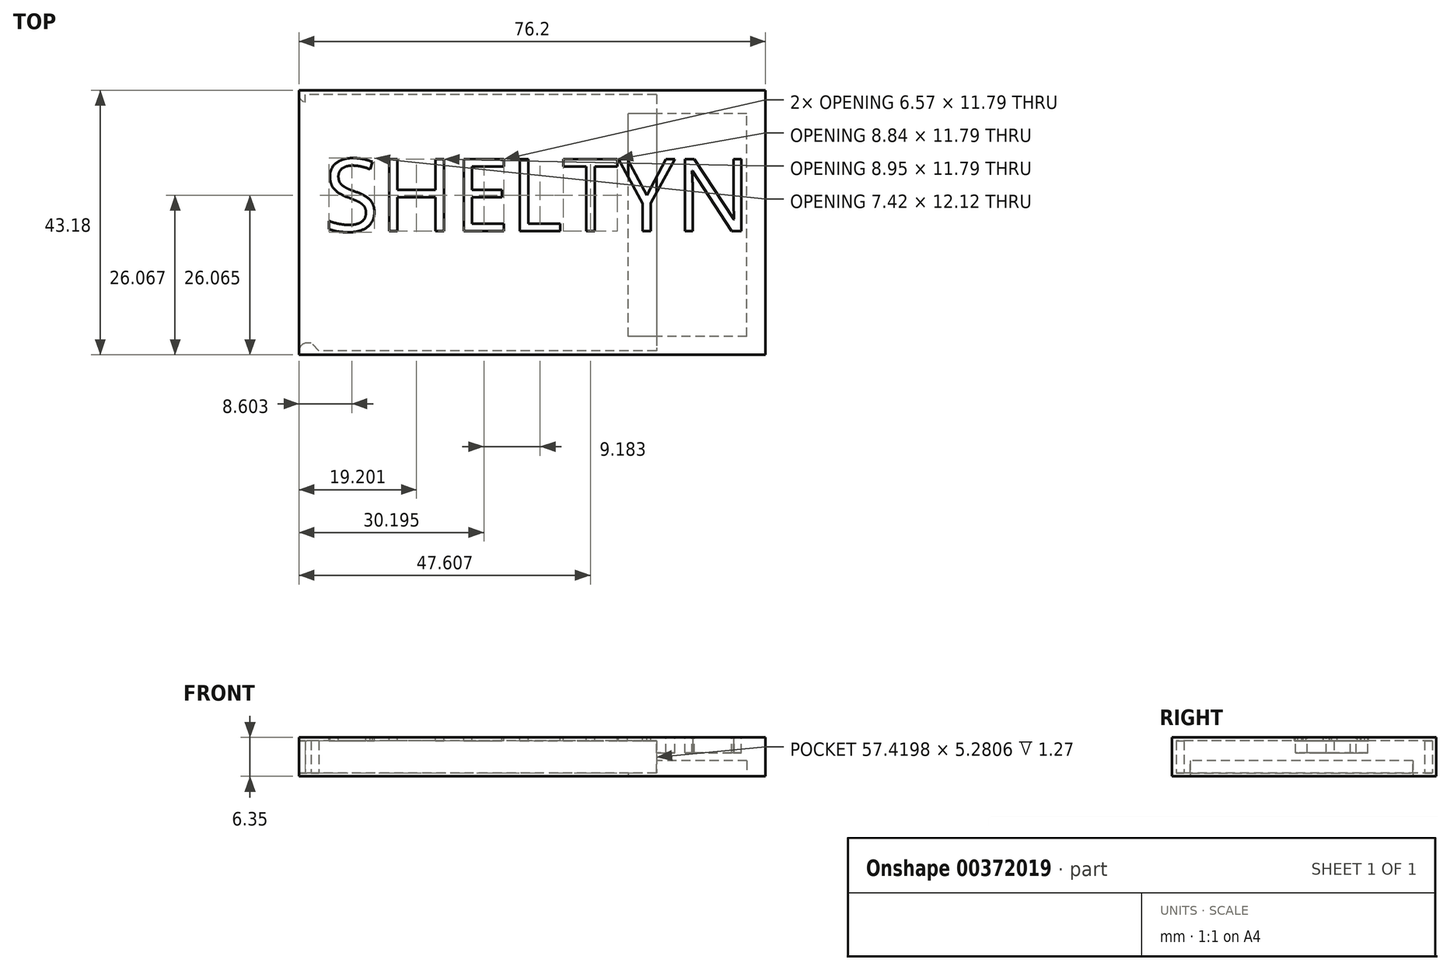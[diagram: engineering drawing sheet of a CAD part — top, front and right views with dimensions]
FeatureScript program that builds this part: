
annotation { "Feature Type Name" : "Feature", "Feature Type Description" : "" }
export const myFeature = defineFeature(function(context is Context, id is Id, definition is map)
    precondition{}
    {
        {
            var Q0;
            Q0=qCreatedBy(makeId("Top.planeOp"),FACE);
            var sketch = newSketch(context, id + "F0", { "sketchPlane" : qUnion([Q0])});
            skLineSegment(sketch, "E0.bottom", {"start": v(-35.13, 22.2) * mm, "end": v(41.07, 22.2) * mm});
            skLineSegment(sketch, "E0.top", {"start": v(-35.13, -20.99) * mm, "end": v(41.07, -20.99) * mm});
            skLineSegment(sketch, "E0.left", {"start": v(-35.13, 22.2) * mm, "end": v(-35.13, -20.99) * mm});
            skLineSegment(sketch, "E0.right", {"start": v(41.07, 22.2) * mm, "end": v(41.07, -20.99) * mm});
            skSolve(sketch);
        }
        {
            var Q0;
            Q0=makeQuery(id+"F0.imprint","IMPRINT",FACE,{"disambiguationData":[TD([[makeQuery(id+"F0.imprint","IMPRINT",EDGE,{"derivedFrom":sQuery(id+"F0.wireOp",EDGE,"E0.bottom")}),-1.0]])]});
            extrude(context, id + "F1", {"entities" : qUnion([Q0]), "depth" : 6.35 * mm});
        }
        {
            var Q0;
            Q0=makeQuery(id+"F1.opExtrude","SWEPT_FACE",FACE,{"disambiguationData":[OSD([sQuery(id+"F0.wireOp",EDGE,"E0.left")])]});
            var sketch = newSketch(context, id + "F2", { "sketchPlane" : qUnion([Q0])});
            skLineSegment(sketch, "E1.bottom", {"start": v(-21.5, 5.8) * mm, "end": v(20.34, 5.8) * mm});
            skLineSegment(sketch, "E1.top", {"start": v(-21.5, 0.5) * mm, "end": v(20.34, 0.5) * mm});
            skLineSegment(sketch, "E1.left", {"start": v(-21.5, 5.8) * mm, "end": v(-21.5, 0.5) * mm});
            skLineSegment(sketch, "E1.right", {"start": v(20.34, 5.8) * mm, "end": v(20.34, 0.5) * mm});
            skSolve(sketch);
        }
        {
            var Q0;
            Q0=makeQuery(id+"F2.imprint","IMPRINT",FACE,{"disambiguationData":[TD([[makeQuery(id+"F2.imprint","IMPRINT",EDGE,{"derivedFrom":sQuery(id+"F2.wireOp",EDGE,"E1.bottom")}),-1.0]])]});
            extrude(context, id + "F3", {"entities" : qUnion([Q0]), "operationType" : NewBodyOperationType.REMOVE, "oppositeDirection" : true, "depth" : 58.42 * mm});
        }
        {
            var Q0;
            Q0=makeQuery(id+"F1.opExtrude","CAP_FACE",FACE,{"disambiguationData":[OSD([sQuery(id+"F0.wireOp",EDGE,"E0.bottom"),sQuery(id+"F0.wireOp",EDGE,"E0.top"),sQuery(id+"F0.wireOp",EDGE,"E0.left"),sQuery(id+"F0.wireOp",EDGE,"E0.right")])],"isStart":true});
            var sketch = newSketch(context, id + "F4", { "sketchPlane" : qUnion([Q0])});
            skLineSegment(sketch, "E2.bottom", {"start": v(38.04, 18.01) * mm, "end": v(18.65, 18.01) * mm});
            skLineSegment(sketch, "E2.top", {"start": v(38.04, -18.38) * mm, "end": v(18.65, -18.38) * mm});
            skLineSegment(sketch, "E2.left", {"start": v(38.04, 18.01) * mm, "end": v(38.04, -18.38) * mm});
            skLineSegment(sketch, "E2.right", {"start": v(18.65, 18.01) * mm, "end": v(18.65, -18.38) * mm});
            skSolve(sketch);
        }
        {
            var Q0;
            Q0=makeQuery(id+"F4.imprint","IMPRINT",FACE,{"disambiguationData":[TD([[makeQuery(id+"F4.imprint","IMPRINT",EDGE,{"derivedFrom":sQuery(id+"F4.wireOp",EDGE,"E2.bottom")}),1.0]])]});
            extrude(context, id + "F5", {"entities" : qUnion([Q0]), "operationType" : NewBodyOperationType.REMOVE, "oppositeDirection" : true, "depth" : 2.54 * mm});
        }
        {
            var Q0;
            Q0=makeQuery(id+"F3.boolean.opBoolean","COPY",FACE,{"derivedFrom":makeQuery(id+"F3.opExtrude","SWEPT_FACE",FACE,{"disambiguationData":[OSD([sQuery(id+"F2.wireOp",EDGE,"E1.left")])]})});
            var sketch = newSketch(context, id + "F6", { "sketchPlane" : qUnion([Q0])});
            skLineSegment(sketch, "E3.bottom", {"start": v(-35.13, 5.8) * mm, "end": v(-34.13, 5.8) * mm});
            skLineSegment(sketch, "E3.top", {"start": v(-35.13, 0.5) * mm, "end": v(-34.13, 0.5) * mm});
            skLineSegment(sketch, "E3.left", {"start": v(-35.13, 5.8) * mm, "end": v(-35.13, 0.5) * mm});
            skLineSegment(sketch, "E3.right", {"start": v(-34.13, 5.8) * mm, "end": v(-34.13, 0.5) * mm});
            skSolve(sketch);
        }
        {
            var Q0;
            Q0=makeQuery(id+"F6.imprint","IMPRINT",FACE,{"disambiguationData":[TD([[makeQuery(id+"F6.imprint","IMPRINT",EDGE,{"derivedFrom":sQuery(id+"F6.wireOp",EDGE,"E3.bottom")}),1.0]])]});
            extrude(context, id + "F7", {"entities" : qUnion([Q0]), "operationType" : NewBodyOperationType.ADD, "depth" : 2.54 * mm});
        }
        {
            var Q0;
            Q0=makeQuery(id+"F7.opExtrude","CAP_EDGE",EDGE,{"disambiguationData":[OSD([sQuery(id+"F6.wireOp",EDGE,"E3.right")])],"isStart":false});
            chamfer(context, id + "F8", {"entities" : qUnion([Q0]), "width" : 1.27 * mm, "tangentPropagation" : true});
        }
        {
            var Q0;
            Q0=makeQuery(id+"F3.boolean.opBoolean","COPY",FACE,{"derivedFrom":makeQuery(id+"F3.opExtrude","SWEPT_FACE",FACE,{"disambiguationData":[OSD([sQuery(id+"F2.wireOp",EDGE,"E1.right")])]})});
            var sketch = newSketch(context, id + "F9", { "sketchPlane" : qUnion([Q0])});
            skLineSegment(sketch, "E4.bottom", {"start": v(35.13, 5.8) * mm, "end": v(31.88, 5.8) * mm});
            skLineSegment(sketch, "E4.top", {"start": v(35.13, 0.5) * mm, "end": v(31.88, 0.5) * mm});
            skLineSegment(sketch, "E4.left", {"start": v(35.13, 5.8) * mm, "end": v(35.13, 0.5) * mm});
            skLineSegment(sketch, "E4.right", {"start": v(31.88, 5.8) * mm, "end": v(31.88, 0.5) * mm});
            skSolve(sketch);
        }
        {
            var Q0;
            Q0=makeQuery(id+"F9.imprint","IMPRINT",FACE,{"disambiguationData":[TD([[makeQuery(id+"F9.imprint","IMPRINT",EDGE,{"derivedFrom":sQuery(id+"F9.wireOp",EDGE,"E4.bottom")}),-1.0]])]});
            extrude(context, id + "F10", {"entities" : qUnion([Q0]), "operationType" : NewBodyOperationType.ADD, "depth" : 1.27 * mm});
        }
        {
            var Q0;
            Q0=makeQuery(id+"F10.opExtrude","CAP_EDGE",EDGE,{"disambiguationData":[OSD([sQuery(id+"F9.wireOp",EDGE,"E4.right")])],"isStart":false});
            chamfer(context, id + "F11", {"entities" : qUnion([Q0]), "width" : 1.27 * mm, "tangentPropagation" : true});
        }
        {
            var Q0;
            Q0=makeQuery(id+"F8.opChamfer","BLEND_EDGE",EDGE,{"blendedFrom":[makeQuery(id+"F7.opExtrude","CAP_EDGE",EDGE,{"disambiguationData":[OSD([sQuery(id+"F6.wireOp",EDGE,"E3.right")])],"isStart":false}),makeQuery(id+"F7.boolean.opBoolean","MERGE",FACE,{"derivedFrom":[makeQuery(id+"F1.opExtrude","SWEPT_FACE",FACE,{"disambiguationData":[OSD([sQuery(id+"F0.wireOp",EDGE,"E0.left")])]}),makeQuery(id+"F7.opExtrude","SWEPT_FACE",FACE,{"disambiguationData":[OSD([sQuery(id+"F6.wireOp",EDGE,"E3.left")])]})]})],"blendedInto":[makeQuery(id+"F7.boolean.opBoolean","MERGE",FACE,{"derivedFrom":[makeQuery(id+"F1.opExtrude","SWEPT_FACE",FACE,{"disambiguationData":[OSD([sQuery(id+"F0.wireOp",EDGE,"E0.left")])]}),makeQuery(id+"F7.opExtrude","SWEPT_FACE",FACE,{"disambiguationData":[OSD([sQuery(id+"F6.wireOp",EDGE,"E3.left")])]})]})]});
            fillet(context, id + "F12", {"entities" : qUnion([Q0]), "radius" : 1.27 * mm, "tangentPropagation" : true, "allowEdgeOverflow" : false});
        }
        {
            var Q0;
            Q0=makeQuery(id+"F10.opExtrude","CAP_EDGE",EDGE,{"disambiguationData":[OSD([sQuery(id+"F9.wireOp",EDGE,"E4.left")])],"isStart":false});
            fillet(context, id + "F13", {"entities" : qUnion([Q0]), "radius" : 1.27 * mm, "tangentPropagation" : true, "allowEdgeOverflow" : false});
        }
        {
            var Q0;
            Q0=makeQuery(id+"F1.opExtrude","CAP_FACE",FACE,{"disambiguationData":[OSD([sQuery(id+"F0.wireOp",EDGE,"E0.bottom"),sQuery(id+"F0.wireOp",EDGE,"E0.top"),sQuery(id+"F0.wireOp",EDGE,"E0.left"),sQuery(id+"F0.wireOp",EDGE,"E0.right")])],"isStart":false});
            var sketch = newSketch(context, id + "F14", { "sketchPlane" : qUnion([Q0])});
            skText(sketch, "E5", { "text": "SHELTYN", "fontName": "OpenSans-Regular.ttf"});
            const initialGuessF14  = {"E5": [-0.03109, -0.00082, 1, 0, 0.01189]};
            skSetInitialGuess(sketch, initialGuessF14);
            skSolve(sketch);
        }
        {
            var Q0;
            Q0 = qSketchRegion(id + "F14", true);
            extrude(context, id + "F15", {"entities" : qUnion([Q0]), "operationType" : NewBodyOperationType.REMOVE, "oppositeDirection" : true, "depth" : 2.54 * mm});
        }
    });
